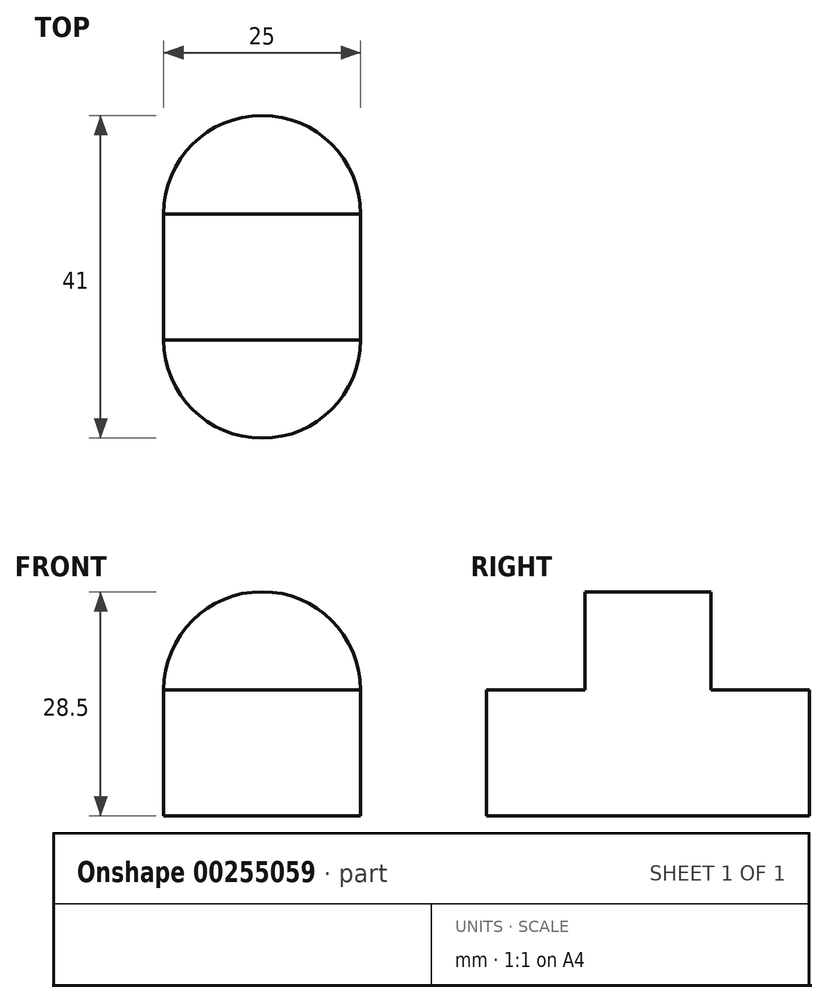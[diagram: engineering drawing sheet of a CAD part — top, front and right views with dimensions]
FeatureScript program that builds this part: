
annotation { "Feature Type Name" : "Feature", "Feature Type Description" : "" }
export const myFeature = defineFeature(function(context is Context, id is Id, definition is map)
    precondition{}
    {
        {
            var Q0;
            Q0=qCreatedBy(makeId("Top.planeOp"),FACE);
            var sketch = newSketch(context, id + "F0", { "sketchPlane" : qUnion([Q0])});
            skCircle(sketch, "E0", {"center": v(0, 0) * mm, "radius": 12.5 * mm});
            skSolve(sketch);
        }
        {
            var Q0;
            Q0 = qSketchRegion(id + "F0", true);
            extrude(context, id + "F1", {"entities" : qUnion([Q0]), "depth" : 16 * mm});
        }
        {
            var Q0;
            Q0=qCreatedBy(makeId("Front.planeOp"),FACE);
            var sketch = newSketch(context, id + "F2", { "sketchPlane" : qUnion([Q0])});
            skCircle(sketch, "E1", {"center": v(0, 16) * mm, "radius": 12.5 * mm});
            skSolve(sketch);
        }
        {
            var Q0;
            Q0 = qSketchRegion(id + "F2", true);
            extrude(context, id + "F3", {"entities" : qUnion([Q0]), "operationType" : NewBodyOperationType.ADD, "depth" : 8 * mm, "hasSecondDirection" : true, "secondDirectionOppositeDirection" : true, "secondDirectionDepth" : 8 * mm});
        }
        {
            var Q0;
            Q0=qCreatedBy(makeId("Top.planeOp"),FACE);
            var sketch = newSketch(context, id + "F4", { "sketchPlane" : qUnion([Q0])});
            skCircle(sketch, "E2", {"center": v(0, 8) * mm, "radius": 12.5 * mm});
            skCircle(sketch, "E3", {"center": v(0, -8) * mm, "radius": 12.5 * mm});
            skLineSegment(sketch, "E4.bottom", {"start": v(-12.5, 8) * mm, "end": v(12.5, 8) * mm});
            skLineSegment(sketch, "E4.top", {"start": v(-12.5, -8) * mm, "end": v(12.5, -8) * mm});
            skLineSegment(sketch, "E4.left", {"start": v(-12.5, 8) * mm, "end": v(-12.5, -8) * mm});
            skLineSegment(sketch, "E4.right", {"start": v(12.5, 8) * mm, "end": v(12.5, -8) * mm});
            skSolve(sketch);
        }
        {
            var Q0;
            Q0 = qSketchRegion(id + "F4", true);
            extrude(context, id + "F5", {"entities" : qUnion([Q0]), "operationType" : NewBodyOperationType.ADD, "depth" : 16 * mm});
        }
    });
